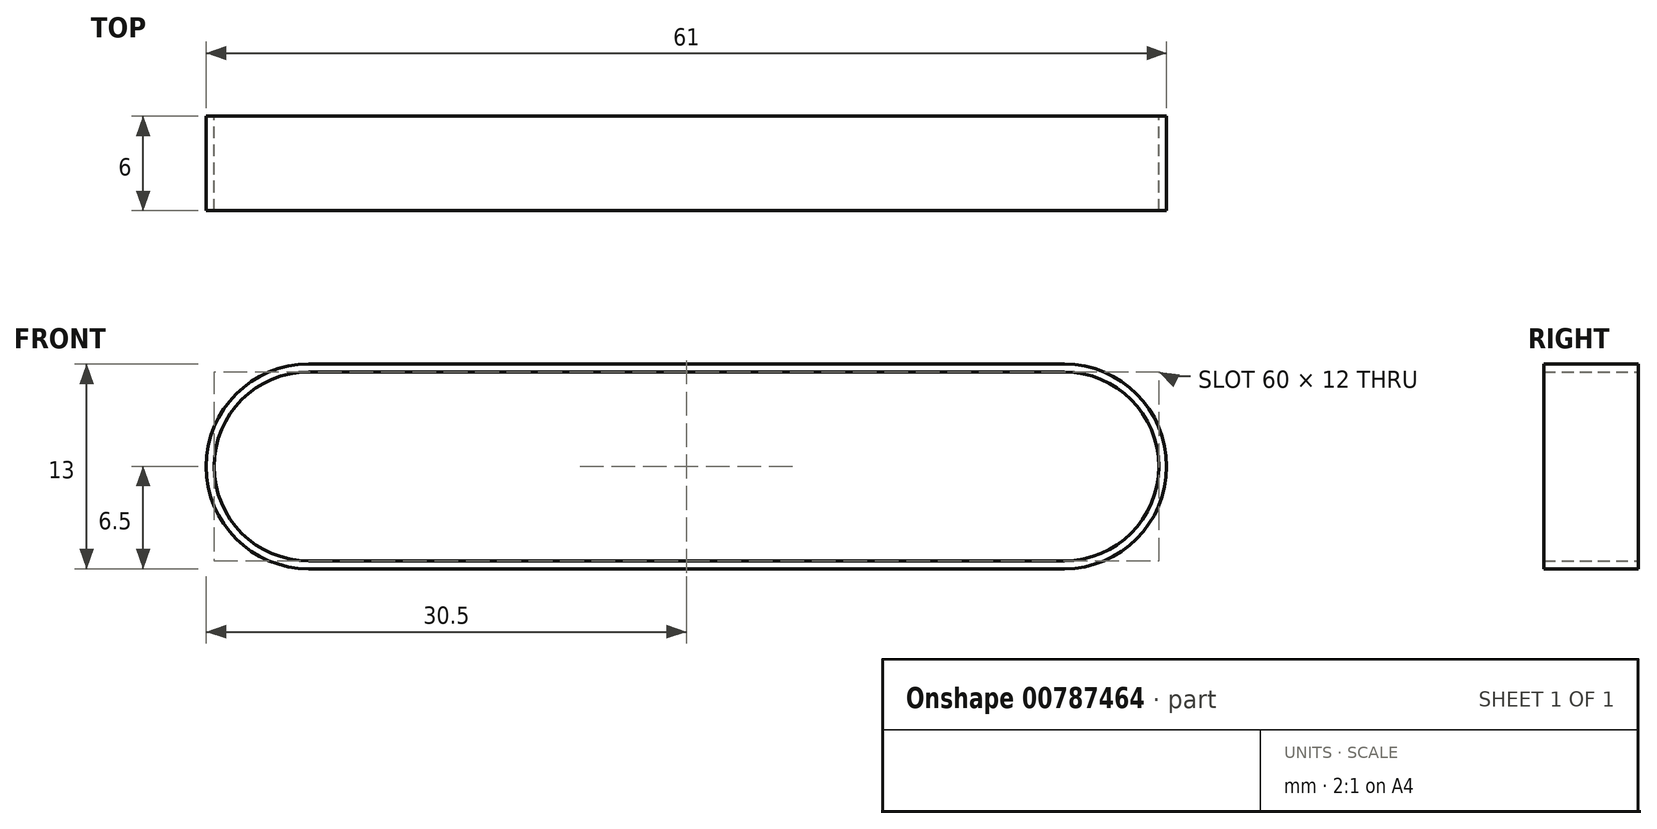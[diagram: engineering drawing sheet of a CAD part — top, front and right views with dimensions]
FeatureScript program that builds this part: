
annotation { "Feature Type Name" : "Feature", "Feature Type Description" : "" }
export const myFeature = defineFeature(function(context is Context, id is Id, definition is map)
    precondition{}
    {
        {
            var Q0;
            Q0=qCreatedBy(makeId("Front.planeOp"),FACE);
            var sketch = newSketch(context, id + "F0", { "sketchPlane" : qUnion([Q0])});
            skLineSegment(sketch, "E0", {"start": v(116.06, 0) * mm, "end": v(254.5, 0) * mm, "construction": true});
            skArc(sketch, "E1", {"start": v(-24, 6.5) * mm, "mid": v(-30.5, 0) * mm, "end": v(-24, -6.5) * mm});
            skLineSegment(sketch, "E2", {"start": v(-24, 6.5) * mm, "end": v(0, 6.5) * mm});
            skLineSegment(sketch, "E3", {"start": v(-24, -6.5) * mm, "end": v(0, -6.5) * mm});
            skArc(sketch, "E4", {"start": v(-24, 6) * mm, "mid": v(-30, 0) * mm, "end": v(-24, -6) * mm});
            skLineSegment(sketch, "E5", {"start": v(-24, -6) * mm, "end": v(0, -6) * mm});
            skLineSegment(sketch, "E6.MirrorCS", {"start": v(69.44, 0) * mm, "end": v(-69, 0) * mm, "construction": true});
            skLineSegment(sketch, "E7", {"start": v(0, 0) * mm, "end": v(0, 27.23) * mm, "construction": true});
            skLineSegment(sketch, "E8", {"start": v(-24, 6) * mm, "end": v(0, 6) * mm});
            skLineSegment(sketch, "E9", {"start": v(0, 6) * mm, "end": v(-0.22, 5.14) * mm});
            skLineSegment(sketch, "E10.MirrorCS", {"start": v(24, 6) * mm, "end": v(0, 6) * mm});
            skLineSegment(sketch, "E11.MirrorCS", {"start": v(24, 6.5) * mm, "end": v(0, 6.5) * mm});
            skArc(sketch, "E12.MirrorCS", {"start": v(24, 6) * mm, "mid": v(30, 0) * mm, "end": v(24, -6) * mm});
            skArc(sketch, "E13.MirrorCS", {"start": v(24, 6.5) * mm, "mid": v(30.5, 0) * mm, "end": v(24, -6.5) * mm});
            skLineSegment(sketch, "E14.MirrorCS", {"start": v(24, -6) * mm, "end": v(0, -6) * mm});
            skLineSegment(sketch, "E15.MirrorCS", {"start": v(24, -6.5) * mm, "end": v(0, -6.5) * mm});
            skSolve(sketch);
        }
        {
            var Q0;
            Q0 = qSketchRegion(id + "F0", true);
            extrude(context, id + "F1", {"entities" : qUnion([Q0]), "depth" : 6 * mm, "offsetDistance" : 25 * mm});
        }
    });
